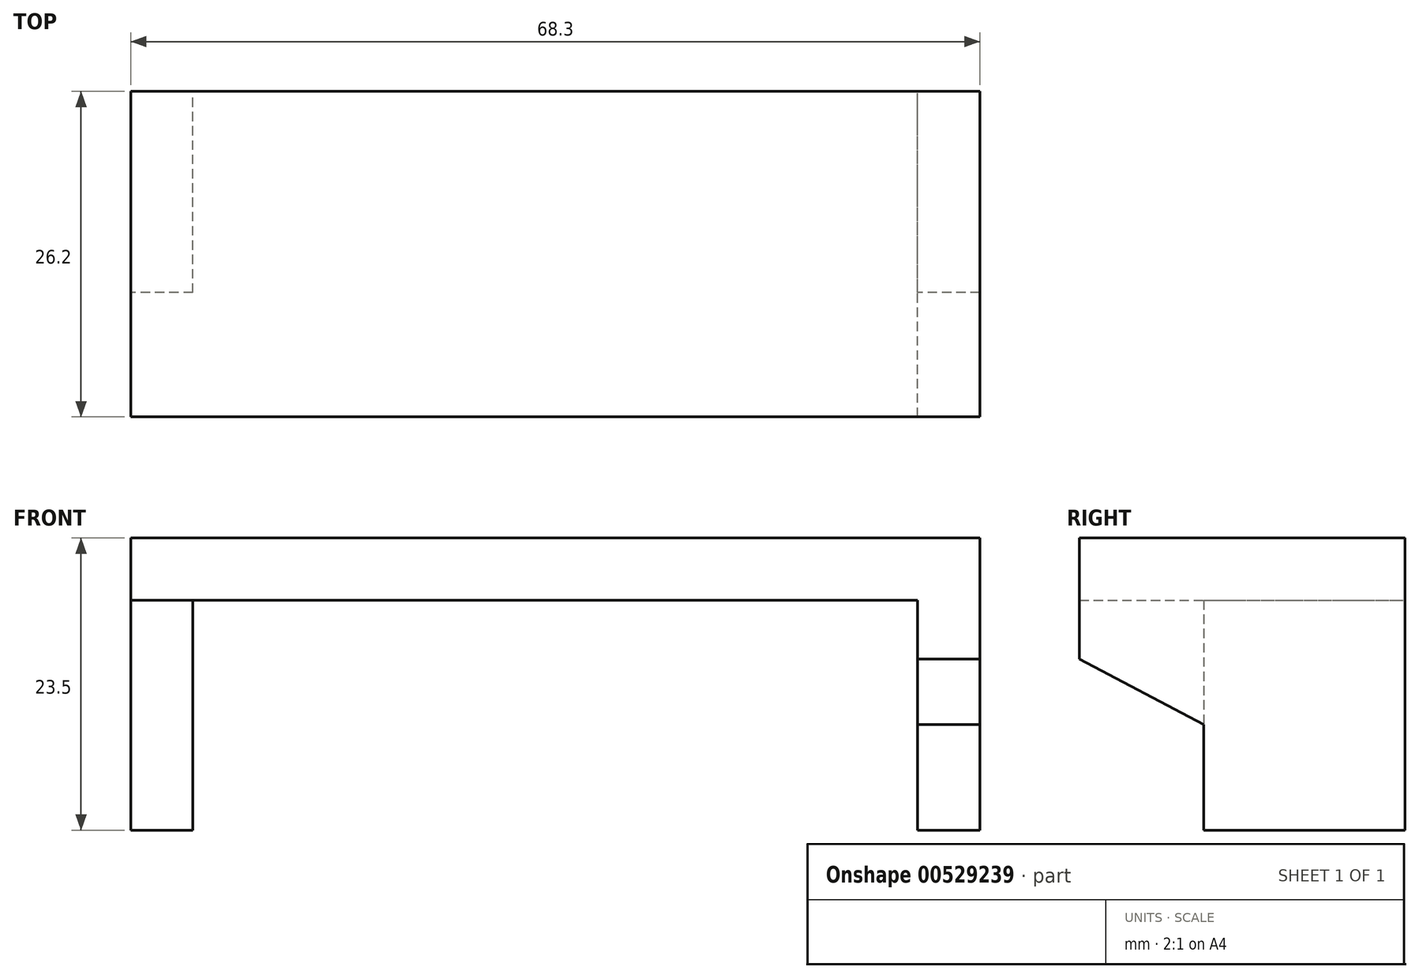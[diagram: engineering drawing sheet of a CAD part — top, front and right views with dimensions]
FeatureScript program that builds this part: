
annotation { "Feature Type Name" : "Feature", "Feature Type Description" : "" }
export const myFeature = defineFeature(function(context is Context, id is Id, definition is map)
    precondition{}
    {
        {
            var Q0;
            Q0=qCreatedBy(makeId("Front.planeOp"),FACE);
            var sketch = newSketch(context, id + "F0", { "sketchPlane" : qUnion([Q0])});
            skLineSegment(sketch, "E0", {"start": v(0, 0) * mm, "end": v(29.15, 0) * mm});
            skLineSegment(sketch, "E1", {"start": v(29.15, 0) * mm, "end": v(29.15, -18.5) * mm});
            skLineSegment(sketch, "E2", {"start": v(29.15, -18.5) * mm, "end": v(34.15, -18.5) * mm});
            skLineSegment(sketch, "E3", {"start": v(34.15, -18.5) * mm, "end": v(34.15, 5) * mm});
            skLineSegment(sketch, "E4", {"start": v(34.15, 5) * mm, "end": v(0, 5) * mm});
            skLineSegment(sketch, "E5", {"start": v(0, -24.2) * mm, "end": v(0, 23.67) * mm, "construction": true});
            skLineSegment(sketch, "E6.MirrorCS", {"start": v(-34.15, 5) * mm, "end": v(0, 5) * mm});
            skLineSegment(sketch, "E7.MirrorCS", {"start": v(0, 0) * mm, "end": v(-29.15, 0) * mm});
            skLineSegment(sketch, "E8.MirrorCS", {"start": v(-29.15, 0) * mm, "end": v(-29.15, -18.5) * mm});
            skLineSegment(sketch, "E9.MirrorCS", {"start": v(-29.15, -18.5) * mm, "end": v(-34.15, -18.5) * mm});
            skLineSegment(sketch, "E10.MirrorCS", {"start": v(-34.15, -18.5) * mm, "end": v(-34.15, 5) * mm});
            skSolve(sketch);
        }
        {
            var Q0;
            Q0=makeQuery(id+"F0.imprint","IMPRINT",FACE,{"disambiguationData":[TD([[makeQuery(id+"F0.imprint","IMPRINT",EDGE,{"derivedFrom":sQuery(id+"F0.wireOp",EDGE,"E0")}),1.0]])]});
            extrude(context, id + "F1", {"entities" : qUnion([Q0]), "depth" : 16.2 * mm, "offsetDistance" : 25 * mm});
        }
        {
            var Q0;
            Q0=makeQuery(id+"F1.opExtrude","CAP_FACE",FACE,{"disambiguationData":[OSD([sQuery(id+"F0.wireOp",EDGE,"E0"),sQuery(id+"F0.wireOp",EDGE,"E1"),sQuery(id+"F0.wireOp",EDGE,"E2"),sQuery(id+"F0.wireOp",EDGE,"E3"),sQuery(id+"F0.wireOp",EDGE,"E4"),sQuery(id+"F0.wireOp",EDGE,"E6.MirrorCS"),sQuery(id+"F0.wireOp",EDGE,"E7.MirrorCS"),sQuery(id+"F0.wireOp",EDGE,"E8.MirrorCS"),sQuery(id+"F0.wireOp",EDGE,"E9.MirrorCS"),sQuery(id+"F0.wireOp",EDGE,"E10.MirrorCS")])],"isStart":false});
            var sketch = newSketch(context, id + "F2", { "sketchPlane" : qUnion([Q0])});
            skLineSegment(sketch, "E11.bottom", {"start": v(-34.15, 5) * mm, "end": v(34.15, 5) * mm});
            skLineSegment(sketch, "E11.top", {"start": v(-34.15, 0) * mm, "end": v(34.15, 0) * mm});
            skLineSegment(sketch, "E11.left", {"start": v(-34.15, 5) * mm, "end": v(-34.15, 0) * mm});
            skLineSegment(sketch, "E11.right", {"start": v(34.15, 5) * mm, "end": v(34.15, 0) * mm});
            skSolve(sketch);
        }
        {
            var Q0;
            Q0=makeQuery(id+"F2.imprint","IMPRINT",FACE,{"disambiguationData":[TD([[makeQuery(id+"F2.imprint","IMPRINT",EDGE,{"derivedFrom":sQuery(id+"F2.wireOp",EDGE,"E11.bottom")}),1.0]])]});
            extrude(context, id + "F3", {"entities" : qUnion([Q0]), "operationType" : NewBodyOperationType.ADD, "depth" : 10 * mm, "offsetDistance" : 25 * mm});
        }
        {
            var Q0;
            {var subQ1=sQuery(id+"F0.wireOp",EDGE,"E1");var subQ4=sQuery(id+"F2.wireOp",EDGE,"E11.top");Q0=makeQuery(id+"F3.boolean.opBoolean","SPLIT",EDGE,{"disambiguationData":[TD([makeQuery(id+"F1.opExtrude","SWEPT_FACE",FACE,{"disambiguationData":[OSD([subQ1])]})])],"derivedFrom":makeQuery(id+"F3.opExtrude","CAP_EDGE",EDGE,{"disambiguationData":[OSD([subQ4])],"isStart":true})});}
            var Q1;
            {var subQ1=sQuery(id+"F0.wireOp",EDGE,"E8.MirrorCS");var subQ4=sQuery(id+"F2.wireOp",EDGE,"E11.top");Q1=makeQuery(id+"F3.boolean.opBoolean","SPLIT",EDGE,{"disambiguationData":[TD([makeQuery(id+"F1.opExtrude","SWEPT_FACE",FACE,{"disambiguationData":[OSD([subQ1])]})])],"derivedFrom":makeQuery(id+"F3.opExtrude","CAP_EDGE",EDGE,{"disambiguationData":[OSD([subQ4])],"isStart":true})});}
            chamfer(context, id + "F4", {"entities" : qUnion([Q0, Q1]), "chamferType" : ChamferType.TWO_OFFSETS, "width1" : 10 * mm, "oppositeDirection" : false, "width2" : 19 * mm, "tangentPropagation" : true});
        }
    });
